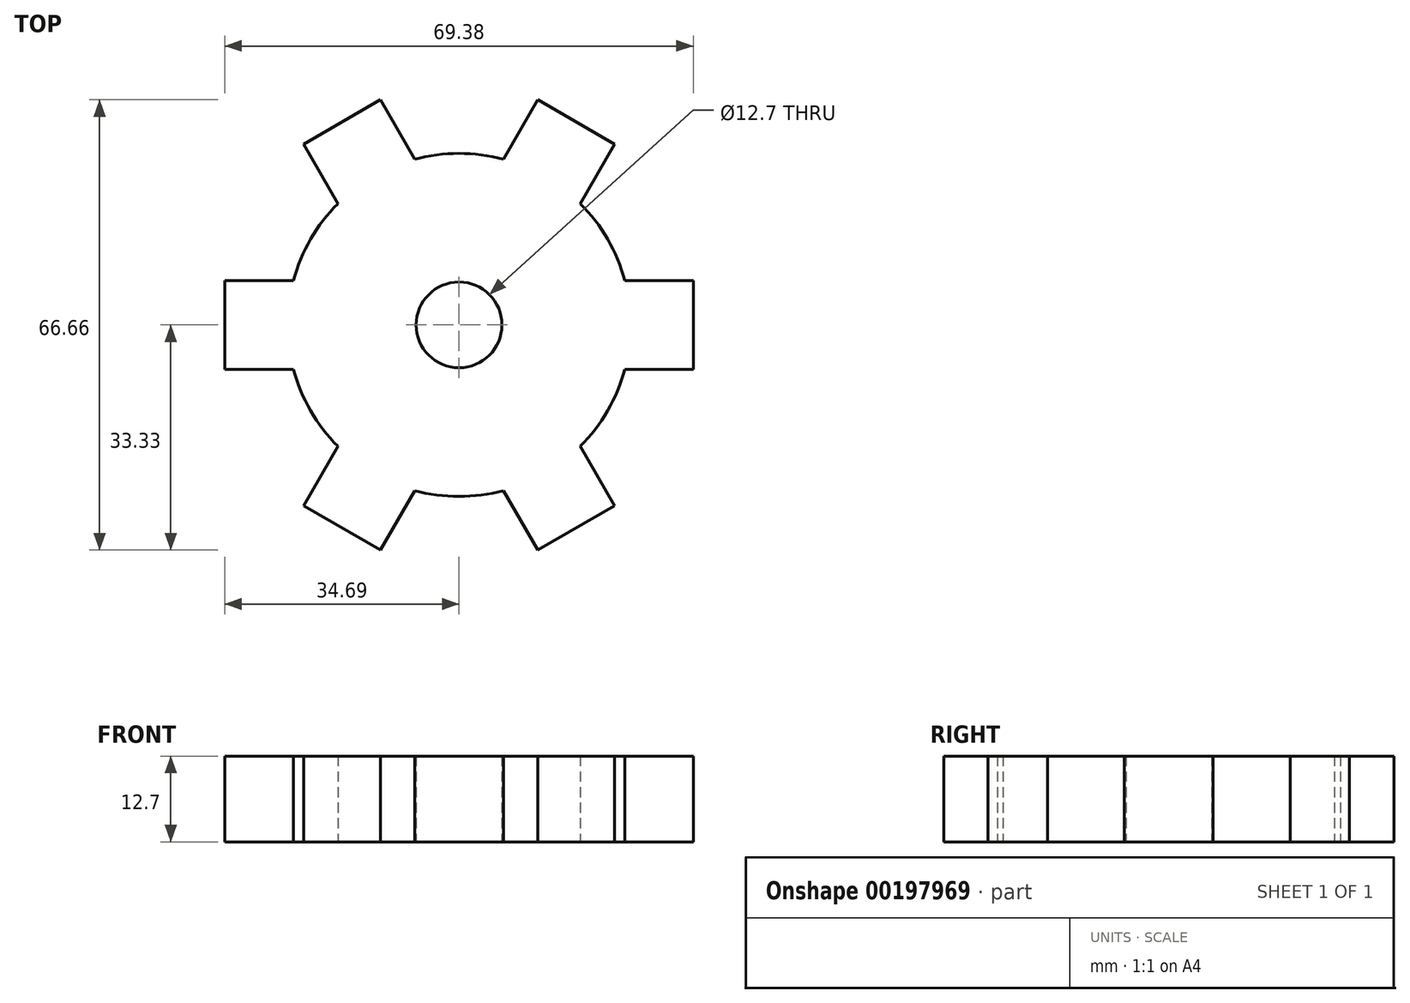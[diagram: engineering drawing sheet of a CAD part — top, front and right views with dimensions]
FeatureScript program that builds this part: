
annotation { "Feature Type Name" : "Feature", "Feature Type Description" : "" }
export const myFeature = defineFeature(function(context is Context, id is Id, definition is map)
    precondition{}
    {
        {
            var Q0;
            Q0=qCreatedBy(makeId("Top.planeOp"),FACE);
            var sketch = newSketch(context, id + "F0", { "sketchPlane" : qUnion([Q0])});
            skCircle(sketch, "E0", {"center": v(0, 0) * mm, "radius": 25.4 * mm});
            skSolve(sketch);
        }
        {
            var Q0;
            Q0 = qSketchRegion(id + "F0", true);
            extrude(context, id + "F1", {"entities" : qUnion([Q0]), "depth" : 12.7 * mm});
        }
        {
            var Q0;
            Q0=makeQuery(id+"F1.opExtrude","CAP_FACE",FACE,{"disambiguationData":[OSD([sQuery(id+"F0.wireOp",EDGE,"E0")])],"isStart":true});
            var sketch = newSketch(context, id + "F2", { "sketchPlane" : qUnion([Q0])});
            skLineSegment(sketch, "E1", {"start": v(0, 0) * mm, "end": v(25.4, 0) * mm});
            skLineSegment(sketch, "E2", {"start": v(0, 0) * mm, "end": v(24.53, 6.57) * mm});
            skLineSegment(sketch, "E3", {"start": v(0, 0) * mm, "end": v(24.53, -6.57) * mm});
            skLineSegment(sketch, "E4", {"start": v(24.53, 6.57) * mm, "end": v(24.53, -6.57) * mm});
            skLineSegment(sketch, "E5", {"start": v(34.7, 6.57) * mm, "end": v(34.7, -6.57) * mm});
            skLineSegment(sketch, "E6", {"start": v(24.53, 6.57) * mm, "end": v(34.7, 6.57) * mm});
            skLineSegment(sketch, "E7", {"start": v(24.53, -6.57) * mm, "end": v(34.7, -6.57) * mm});
            skSolve(sketch);
        }
        {
            var Q0;
            Q0 = qSketchRegion(id + "F2", true);
            extrude(context, id + "F3", {"entities" : qUnion([Q0]), "operationType" : NewBodyOperationType.ADD, "oppositeDirection" : true, "depth" : 12.7 * mm});
        }
        {
            var Q0;
            Q0=qCreatedBy(makeId("Right.planeOp"),FACE);
            var sketch = newSketch(context, id + "F4", { "sketchPlane" : qUnion([Q0])});
            skLineSegment(sketch, "E8", {"start": v(0, 0) * mm, "end": v(0, 61.1) * mm});
            skSolve(sketch);
        }
        {
            var Q0;
            Q0=makeQuery(id+"F1.opExtrude","SWEPT_BODY",BODY,{"disambiguationData":[OSD([sQuery(id+"F0.wireOp",EDGE,"E0")])]});
            var Q1;
            Q1=sQuery(id+"F4.wireOp",EDGE,"E8");
            circularPattern(context, id + "F5", {"operationType" : NewBodyOperationType.ADD, "entities" : qUnion([Q0]), "axis" : qUnion([Q1]), "angle" : 360 * degree, "instanceCount" : 6, "equalSpace" : true});
        }
        {
            var Q0;
            {var subQ0=makeQuery(id+"F3.boolean.opBoolean","MERGE",FACE,{"derivedFrom":[makeQuery(id+"F1.opExtrude","CAP_FACE",FACE,{"disambiguationData":[OSD([sQuery(id+"F0.wireOp",EDGE,"E0")])],"isStart":true}),makeQuery(id+"F3.opExtrude","CAP_FACE",FACE,{"disambiguationData":[OSD([sQuery(id+"F2.wireOp",EDGE,"E2"),sQuery(id+"F2.wireOp",EDGE,"E3"),sQuery(id+"F2.wireOp",EDGE,"E5"),sQuery(id+"F2.wireOp",EDGE,"E6"),sQuery(id+"F2.wireOp",EDGE,"E7")])],"isStart":true})]});Q0=makeQuery(id+"F5.boolean.opBoolean","MERGE",FACE,{"derivedFrom":[subQ0,makeQuery(id+"F5.opPattern","COPY",FACE,{"derivedFrom":subQ0,"instanceName":"1"}),makeQuery(id+"F5.opPattern","COPY",FACE,{"derivedFrom":subQ0,"instanceName":"2"}),makeQuery(id+"F5.opPattern","COPY",FACE,{"derivedFrom":subQ0,"instanceName":"3"}),makeQuery(id+"F5.opPattern","COPY",FACE,{"derivedFrom":subQ0,"instanceName":"4"}),makeQuery(id+"F5.opPattern","COPY",FACE,{"derivedFrom":subQ0,"instanceName":"5"})]});}
            var sketch = newSketch(context, id + "F6", { "sketchPlane" : qUnion([Q0])});
            skCircle(sketch, "E9", {"center": v(0, 0) * mm, "radius": 6.35 * mm});
            skSolve(sketch);
        }
        {
            var Q0;
            Q0=makeQuery(id+"F6.imprint","IMPRINT",FACE,{"disambiguationData":[TD([[makeQuery(id+"F6.imprint","IMPRINT",EDGE,{"derivedFrom":sQuery(id+"F6.wireOp",EDGE,"E9")}),1.0]])]});
            extrude(context, id + "F7", {"entities" : qUnion([Q0]), "operationType" : NewBodyOperationType.REMOVE, "oppositeDirection" : true, "depth" : 25.4 * mm});
        }
    });
